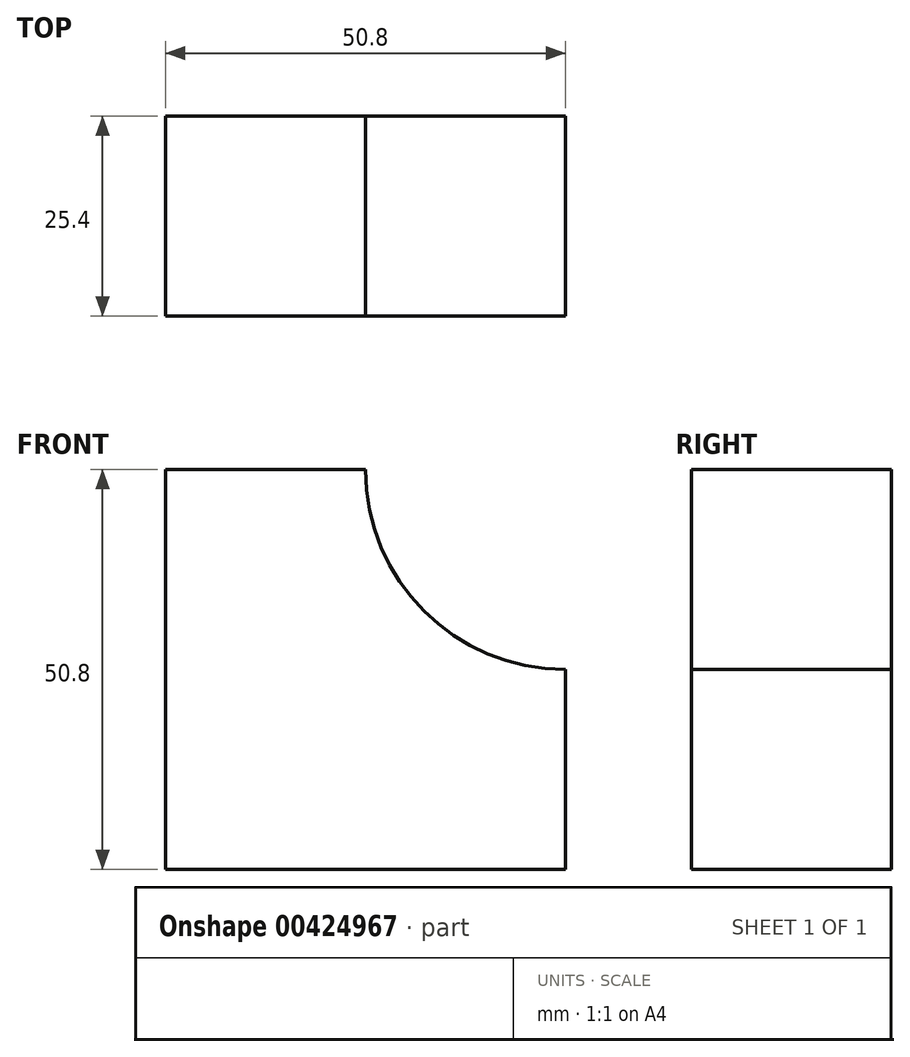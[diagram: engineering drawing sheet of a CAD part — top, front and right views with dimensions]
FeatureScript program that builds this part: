
annotation { "Feature Type Name" : "Feature", "Feature Type Description" : "" }
export const myFeature = defineFeature(function(context is Context, id is Id, definition is map)
    precondition{}
    {
        {
            var Q0;
            Q0=qCreatedBy(makeId("Front.planeOp"),FACE);
            var sketch = newSketch(context, id + "F0", { "sketchPlane" : qUnion([Q0])});
            skLineSegment(sketch, "E0", {"start": v(0, 0) * mm, "end": v(-50.8, 0) * mm});
            skLineSegment(sketch, "E1", {"start": v(-50.8, 0) * mm, "end": v(-50.8, 50.8) * mm});
            skLineSegment(sketch, "E2", {"start": v(-50.8, 50.8) * mm, "end": v(-25.4, 50.8) * mm});
            skLineSegment(sketch, "E3", {"start": v(0, 0) * mm, "end": v(0, 25.4) * mm});
            skArc(sketch, "E4", {"start": v(-25.4, 50.8) * mm, "mid": v(-17.96, 32.84) * mm, "end": v(0, 25.4) * mm});
            skSolve(sketch);
        }
        {
            var Q0;
            Q0 = qSketchRegion(id + "F0", true);
            extrude(context, id + "F1", {"entities" : qUnion([Q0]), "depth" : 25.4 * mm});
        }
    });
